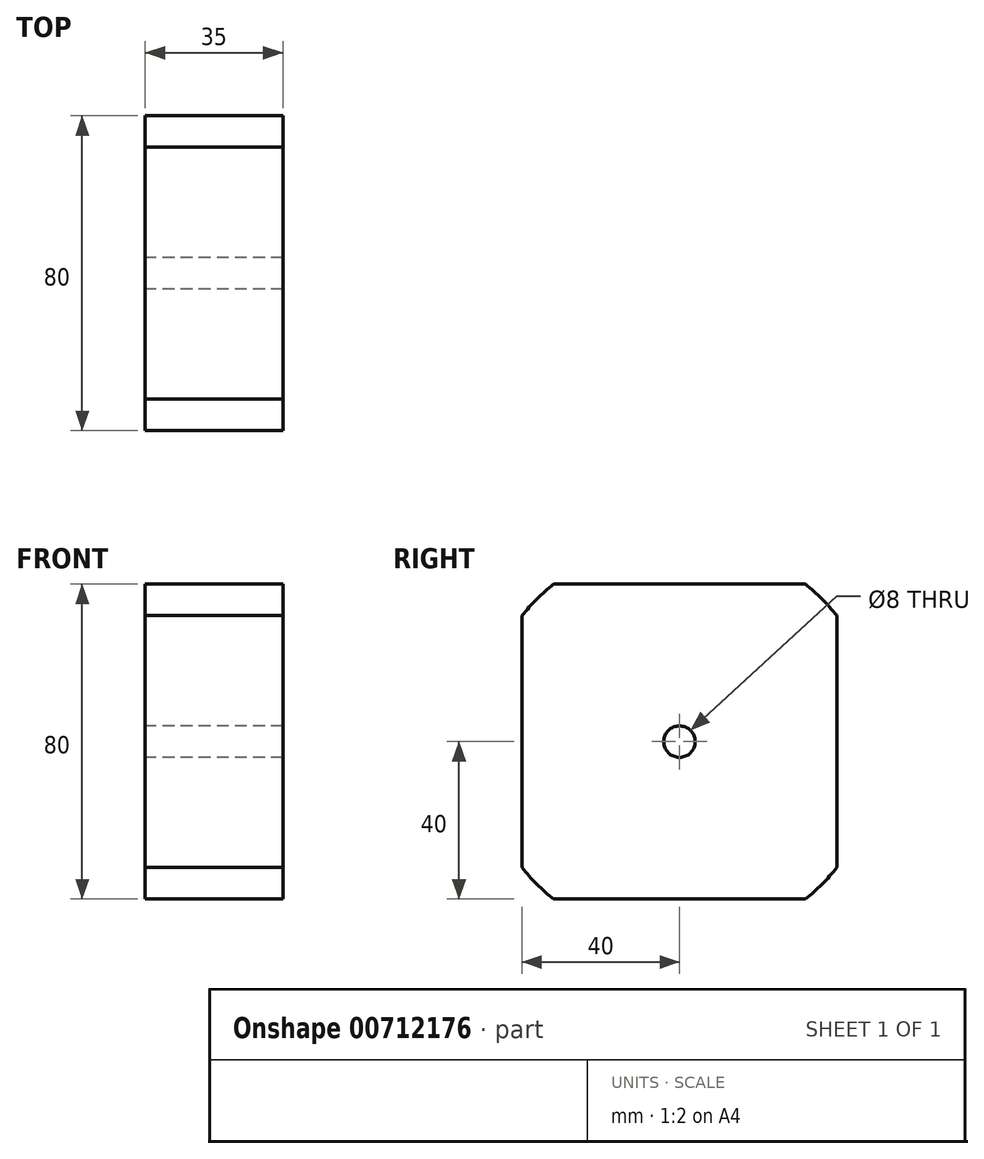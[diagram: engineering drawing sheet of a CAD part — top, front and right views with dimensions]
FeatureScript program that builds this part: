
annotation { "Feature Type Name" : "Feature", "Feature Type Description" : "" }
export const myFeature = defineFeature(function(context is Context, id is Id, definition is map)
    precondition{}
    {
        {
            var Q0;
            Q0=qCreatedBy(makeId("Right.planeOp"),FACE);
            var sketch = newSketch(context, id + "F0", { "sketchPlane" : qUnion([Q0])});
            skLineSegment(sketch, "E0.bottom", {"start": v(-40, 40) * mm, "end": v(40, 40) * mm});
            skLineSegment(sketch, "E0.top", {"start": v(-40, -40) * mm, "end": v(40, -40) * mm});
            skLineSegment(sketch, "E0.left", {"start": v(-40, 40) * mm, "end": v(-40, -40) * mm});
            skLineSegment(sketch, "E0.right", {"start": v(40, 40) * mm, "end": v(40, -40) * mm});
            skPoint(sketch, "E0.middle", {"position": v(0, 0) * mm});
            skSolve(sketch);
        }
        {
            var Q0;
            Q0=qSketchRegion(id+"F0",true);
            extrude(context, id + "F1", {"entities" : qUnion([Q0]), "depth" : 35 * mm, "offsetDistance" : 25 * mm});
        }
        {
            var Q0;
            Q0=makeQuery(id+"F1.opExtrude","CAP_FACE",FACE,{"disambiguationData":[OSD([sQuery(id+"F0.wireOp",EDGE,"E0.bottom"),sQuery(id+"F0.wireOp",EDGE,"E0.top"),sQuery(id+"F0.wireOp",EDGE,"E0.left"),sQuery(id+"F0.wireOp",EDGE,"E0.right")])],"isStart":false});
            var sketch = newSketch(context, id + "F2", { "sketchPlane" : qUnion([Q0])});
            skArc(sketch, "E1", {"start": v(-32, 40) * mm, "mid": v(-36.22, 36.22) * mm, "end": v(-40, 32) * mm});
            skLineSegment(sketch, "E2", {"start": v(-40, 40) * mm, "end": v(-40, 32) * mm});
            skLineSegment(sketch, "E3", {"start": v(-40, 40) * mm, "end": v(-32, 40) * mm});
            skArc(sketch, "E4.1.0", {"start": v(-40, -32) * mm, "mid": v(-36.22, -36.22) * mm, "end": v(-32, -40) * mm});
            skLineSegment(sketch, "E4.1.1", {"start": v(-40, -40) * mm, "end": v(-32, -40) * mm});
            skLineSegment(sketch, "E4.1.2", {"start": v(-40, -40) * mm, "end": v(-40, -32) * mm});
            skArc(sketch, "E4.2.0", {"start": v(32, -40) * mm, "mid": v(36.22, -36.22) * mm, "end": v(40, -32) * mm});
            skLineSegment(sketch, "E4.2.1", {"start": v(40, -40) * mm, "end": v(40, -32) * mm});
            skLineSegment(sketch, "E4.2.2", {"start": v(40, -40) * mm, "end": v(32, -40) * mm});
            skArc(sketch, "E4.3.0", {"start": v(40, 32) * mm, "mid": v(36.22, 36.22) * mm, "end": v(32, 40) * mm});
            skLineSegment(sketch, "E4.3.1", {"start": v(40, 40) * mm, "end": v(32, 40) * mm});
            skLineSegment(sketch, "E4.3.2", {"start": v(40, 40) * mm, "end": v(40, 32) * mm});
            skSolve(sketch);
        }
        {
            var Q0;
            Q0=qSketchRegion(id+"F2",true);
            extrude(context, id + "F3", {"entities" : qUnion([Q0]), "operationType" : NewBodyOperationType.REMOVE, "endBound" : BoundingType.THROUGH_ALL, "oppositeDirection" : true, "depth" : 25 * mm, "offsetDistance" : 25 * mm});
        }
        {
            var Q0;
            Q0=makeQuery(id+"F1.opExtrude","CAP_FACE",FACE,{"disambiguationData":[OSD([sQuery(id+"F0.wireOp",EDGE,"E0.bottom"),sQuery(id+"F0.wireOp",EDGE,"E0.top"),sQuery(id+"F0.wireOp",EDGE,"E0.left"),sQuery(id+"F0.wireOp",EDGE,"E0.right")])],"isStart":true});
            var sketch = newSketch(context, id + "F4", { "sketchPlane" : qUnion([Q0])});
            skCircle(sketch, "E5", {"center": v(0, 0) * mm, "radius": 4 * mm});
            skSolve(sketch);
        }
        {
            var Q0;
            Q0=qSketchRegion(id+"F4",true);
            extrude(context, id + "F5", {"entities" : qUnion([Q0]), "operationType" : NewBodyOperationType.REMOVE, "endBound" : BoundingType.THROUGH_ALL, "oppositeDirection" : true, "depth" : 25 * mm, "offsetDistance" : 25 * mm});
        }
    });
